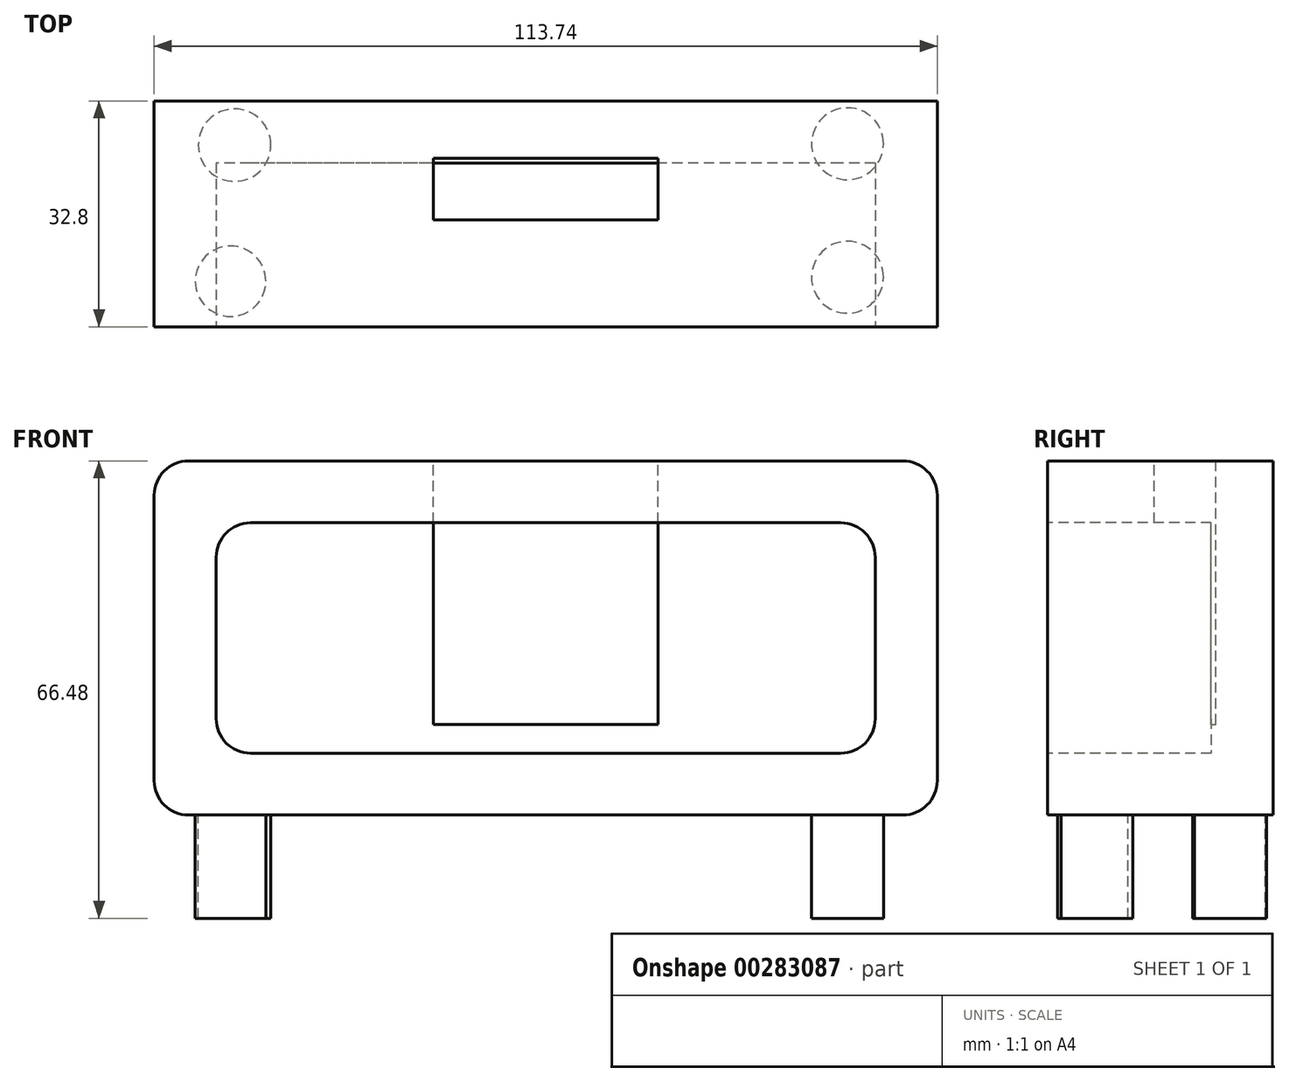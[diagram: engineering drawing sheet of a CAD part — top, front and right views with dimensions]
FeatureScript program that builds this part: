
annotation { "Feature Type Name" : "Feature", "Feature Type Description" : "" }
export const myFeature = defineFeature(function(context is Context, id is Id, definition is map)
    precondition{}
    {
        {
            var Q0;
            Q0=qCreatedBy(makeId("Front.planeOp"),FACE);
            var sketch = newSketch(context, id + "F0", { "sketchPlane" : qUnion([Q0])});
            skLineSegment(sketch, "E0.bottom", {"start": v(56.87, -25.74) * mm, "end": v(-56.87, -25.74) * mm});
            skLineSegment(sketch, "E0.top", {"start": v(56.87, 25.74) * mm, "end": v(-56.87, 25.74) * mm});
            skLineSegment(sketch, "E0.left", {"start": v(56.87, -25.74) * mm, "end": v(56.87, 25.74) * mm});
            skLineSegment(sketch, "E0.right", {"start": v(-56.87, -25.74) * mm, "end": v(-56.87, 25.74) * mm});
            skPoint(sketch, "E0.middle", {"position": v(0, 0) * mm});
            skSolve(sketch);
        }
        {
            var Q0;
            Q0=makeQuery(id+"F0.imprint","IMPRINT",FACE,{"disambiguationData":[TD([[makeQuery(id+"F0.imprint","IMPRINT",EDGE,{"derivedFrom":sQuery(id+"F0.wireOp",EDGE,"E0.bottom")}),-1.0]])]});
            extrude(context, id + "F1", {"entities" : qUnion([Q0]), "depth" : 32.8 * mm});
        }
        {
            var Q0;
            Q0=makeQuery(id+"F1.opExtrude","SWEPT_EDGE",EDGE,{"disambiguationData":[OSD([sQuery(id+"F0.wireOp",EDGE,"E0.top"),sQuery(id+"F0.wireOp",EDGE,"E0.left")])]});
            var Q1;
            Q1=makeQuery(id+"F1.opExtrude","SWEPT_EDGE",EDGE,{"disambiguationData":[OSD([sQuery(id+"F0.wireOp",EDGE,"E0.bottom"),sQuery(id+"F0.wireOp",EDGE,"E0.left")])]});
            var Q2;
            Q2=makeQuery(id+"F1.opExtrude","SWEPT_EDGE",EDGE,{"disambiguationData":[OSD([sQuery(id+"F0.wireOp",EDGE,"E0.bottom"),sQuery(id+"F0.wireOp",EDGE,"E0.right")])]});
            var Q3;
            Q3=makeQuery(id+"F1.opExtrude","SWEPT_EDGE",EDGE,{"disambiguationData":[OSD([sQuery(id+"F0.wireOp",EDGE,"E0.top"),sQuery(id+"F0.wireOp",EDGE,"E0.right")])]});
            fillet(context, id + "F2", {"entities" : qUnion([Q0, Q1, Q2, Q3]), "radius" : 5 * mm, "tangentPropagation" : true, "allowEdgeOverflow" : false});
        }
        {
            var Q0;
            Q0=makeQuery(id+"F1.opExtrude","CAP_FACE",FACE,{"disambiguationData":[OSD([sQuery(id+"F0.wireOp",EDGE,"E0.bottom"),sQuery(id+"F0.wireOp",EDGE,"E0.top"),sQuery(id+"F0.wireOp",EDGE,"E0.left"),sQuery(id+"F0.wireOp",EDGE,"E0.right")])],"isStart":false});
            shell(context, id + "F3", {"entities" : qUnion([Q0]), "thickness" : 9 * mm});
        }
        {
            var Q0;
            Q0=makeQuery(id+"F1.opExtrude","SWEPT_FACE",FACE,{"disambiguationData":[OSD([sQuery(id+"F0.wireOp",EDGE,"E0.top")])]});
            var sketch = newSketch(context, id + "F4", { "sketchPlane" : qUnion([Q0])});
            skLineSegment(sketch, "E1.bottom", {"start": v(16.3, -17.26) * mm, "end": v(-16.3, -17.26) * mm});
            skLineSegment(sketch, "E1.top", {"start": v(16.3, -8.34) * mm, "end": v(-16.3, -8.34) * mm});
            skLineSegment(sketch, "E1.left", {"start": v(16.3, -17.26) * mm, "end": v(16.3, -8.34) * mm});
            skLineSegment(sketch, "E1.right", {"start": v(-16.3, -17.26) * mm, "end": v(-16.3, -8.34) * mm});
            skPoint(sketch, "E1.middle", {"position": v(0, -12.8) * mm});
            skSolve(sketch);
        }
        {
            var Q0;
            Q0 = qSketchRegion(id + "F4", true);
            extrude(context, id + "F5", {"entities" : qUnion([Q0]), "operationType" : NewBodyOperationType.REMOVE, "oppositeDirection" : true, "depth" : 38.3 * mm});
        }
        {
            var Q0;
            Q0=makeQuery(id+"F3.opShell","OFFSET_EDGE",EDGE,{"disambiguationData":[OSD([sQuery(id+"F0.wireOp",EDGE,"E0.top"),sQuery(id+"F0.wireOp",EDGE,"E0.right")])]});
            var Q1;
            Q1=makeQuery(id+"F3.opShell","OFFSET_EDGE",EDGE,{"disambiguationData":[OSD([sQuery(id+"F0.wireOp",EDGE,"E0.bottom"),sQuery(id+"F0.wireOp",EDGE,"E0.right")])]});
            var Q2;
            Q2=makeQuery(id+"F3.opShell","OFFSET_EDGE",EDGE,{"disambiguationData":[OSD([sQuery(id+"F0.wireOp",EDGE,"E0.bottom"),sQuery(id+"F0.wireOp",EDGE,"E0.left")])]});
            var Q3;
            Q3=makeQuery(id+"F3.opShell","OFFSET_EDGE",EDGE,{"disambiguationData":[OSD([sQuery(id+"F0.wireOp",EDGE,"E0.top"),sQuery(id+"F0.wireOp",EDGE,"E0.left")])]});
            fillet(context, id + "F6", {"entities" : qUnion([Q0, Q1, Q2, Q3]), "radius" : 5 * mm, "tangentPropagation" : true, "allowEdgeOverflow" : false});
        }
        {
            var Q0;
            Q0=makeQuery(id+"F1.opExtrude","SWEPT_FACE",FACE,{"disambiguationData":[OSD([sQuery(id+"F0.wireOp",EDGE,"E0.bottom")])]});
            var sketch = newSketch(context, id + "F7", { "sketchPlane" : qUnion([Q0])});
            skCircle(sketch, "E2", {"center": v(-45.78, 26.19) * mm, "radius": 5.12 * mm});
            skCircle(sketch, "E3", {"center": v(-45.2, 6.4) * mm, "radius": 5.27 * mm});
            skCircle(sketch, "E4", {"center": v(43.84, 25.6) * mm, "radius": 5.22 * mm});
            skCircle(sketch, "E5", {"center": v(43.84, 6.2) * mm, "radius": 5.22 * mm});
            skSolve(sketch);
        }
        {
            var Q0;
            Q0=makeQuery(id+"F7.imprint","IMPRINT",FACE,{"disambiguationData":[TD([[makeQuery(id+"F7.imprint","IMPRINT",EDGE,{"derivedFrom":sQuery(id+"F7.wireOp",EDGE,"E3")}),1.0]])]});
            var Q1;
            Q1=makeQuery(id+"F7.imprint","IMPRINT",FACE,{"disambiguationData":[TD([[makeQuery(id+"F7.imprint","IMPRINT",EDGE,{"derivedFrom":sQuery(id+"F7.wireOp",EDGE,"E2")}),1.0]])]});
            var Q2;
            Q2=makeQuery(id+"F7.imprint","IMPRINT",FACE,{"disambiguationData":[TD([[makeQuery(id+"F7.imprint","IMPRINT",EDGE,{"derivedFrom":sQuery(id+"F7.wireOp",EDGE,"E5")}),1.0]])]});
            var Q3;
            Q3=makeQuery(id+"F7.imprint","IMPRINT",FACE,{"disambiguationData":[TD([[makeQuery(id+"F7.imprint","IMPRINT",EDGE,{"derivedFrom":sQuery(id+"F7.wireOp",EDGE,"E4")}),1.0]])]});
            extrude(context, id + "F8", {"entities" : qUnion([Q0, Q1, Q2, Q3]), "operationType" : NewBodyOperationType.ADD, "depth" : 15 * mm});
        }
    });
